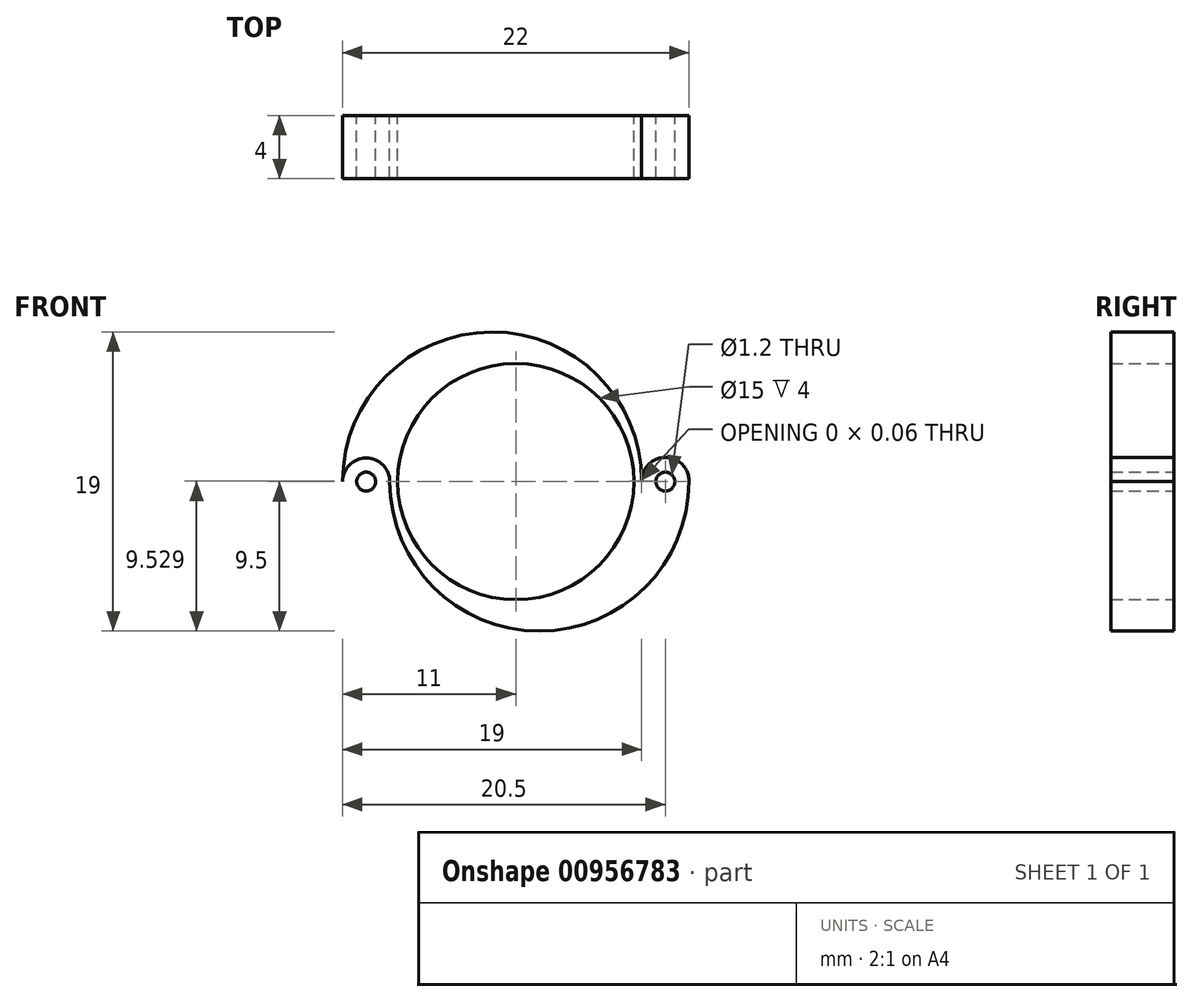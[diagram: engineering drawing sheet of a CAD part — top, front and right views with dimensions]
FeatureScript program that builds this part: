
annotation { "Feature Type Name" : "Feature", "Feature Type Description" : "" }
export const myFeature = defineFeature(function(context is Context, id is Id, definition is map)
    precondition{}
    {
        {
            var Q0;
            Q0=qCreatedBy(makeId("Front.planeOp"),FACE);
            var sketch = newSketch(context, id + "F0", { "sketchPlane" : qUnion([Q0])});
            skLineSegment(sketch, "E0", {"start": v(8, 0) * mm, "end": v(8, 0) * mm});
            skLineSegment(sketch, "E1", {"start": v(11, 0) * mm, "end": v(11, 0) * mm});
            skPoint(sketch, "E2.center.orphan", {"position": v(-9.5, 0) * mm});
            skArc(sketch, "E3", {"start": v(-8, 0) * mm, "mid": v(-9.5, 1.5) * mm, "end": v(-11, 0) * mm});
            skArc(sketch, "E4", {"start": v(8, 0) * mm, "mid": v(8, 0.03) * mm, "end": v(8, 0.06) * mm});
            skPoint(sketch, "E5.center.orphan", {"position": v(9.5, 0) * mm});
            skPoint(sketch, "E6.center.orphan", {"position": v(-1.5, 0) * mm});
            skArc(sketch, "E7", {"start": v(8, 0) * mm, "mid": v(-1.5, 9.5) * mm, "end": v(-11, 0) * mm});
            skCircle(sketch, "E8", {"center": v(-9.5, 0) * mm, "radius": 0.6 * mm});
            skPoint(sketch, "E9.1.0", {"position": v(1.5, 0) * mm});
            skLineSegment(sketch, "E9.1.2", {"start": v(-8, 0) * mm, "end": v(-8, 0) * mm});
            skPoint(sketch, "E9.1.4", {"position": v(9.5, 0) * mm});
            skArc(sketch, "E9.1.5", {"start": v(-8, 0) * mm, "mid": v(1.5, -9.5) * mm, "end": v(11, 0) * mm});
            skCircle(sketch, "E9.1.6", {"center": v(9.5, 0) * mm, "radius": 0.6 * mm});
            skLineSegment(sketch, "E9.1.7", {"start": v(-8, 0) * mm, "end": v(-8, 0) * mm});
            skArc(sketch, "E10", {"start": v(11, 0) * mm, "mid": v(9.5, 1.53) * mm, "end": v(8, 0) * mm});
            skCircle(sketch, "E11", {"center": v(0, 0) * mm, "radius": 7.5 * mm});
            skSolve(sketch);
        }
        {
            var Q0;
            Q0 = qSketchRegion(id + "F0", true);
            extrude(context, id + "F1", {"entities" : qUnion([Q0]), "depth" : 4 * mm, "offsetDistance" : 25 * mm});
        }
    });
